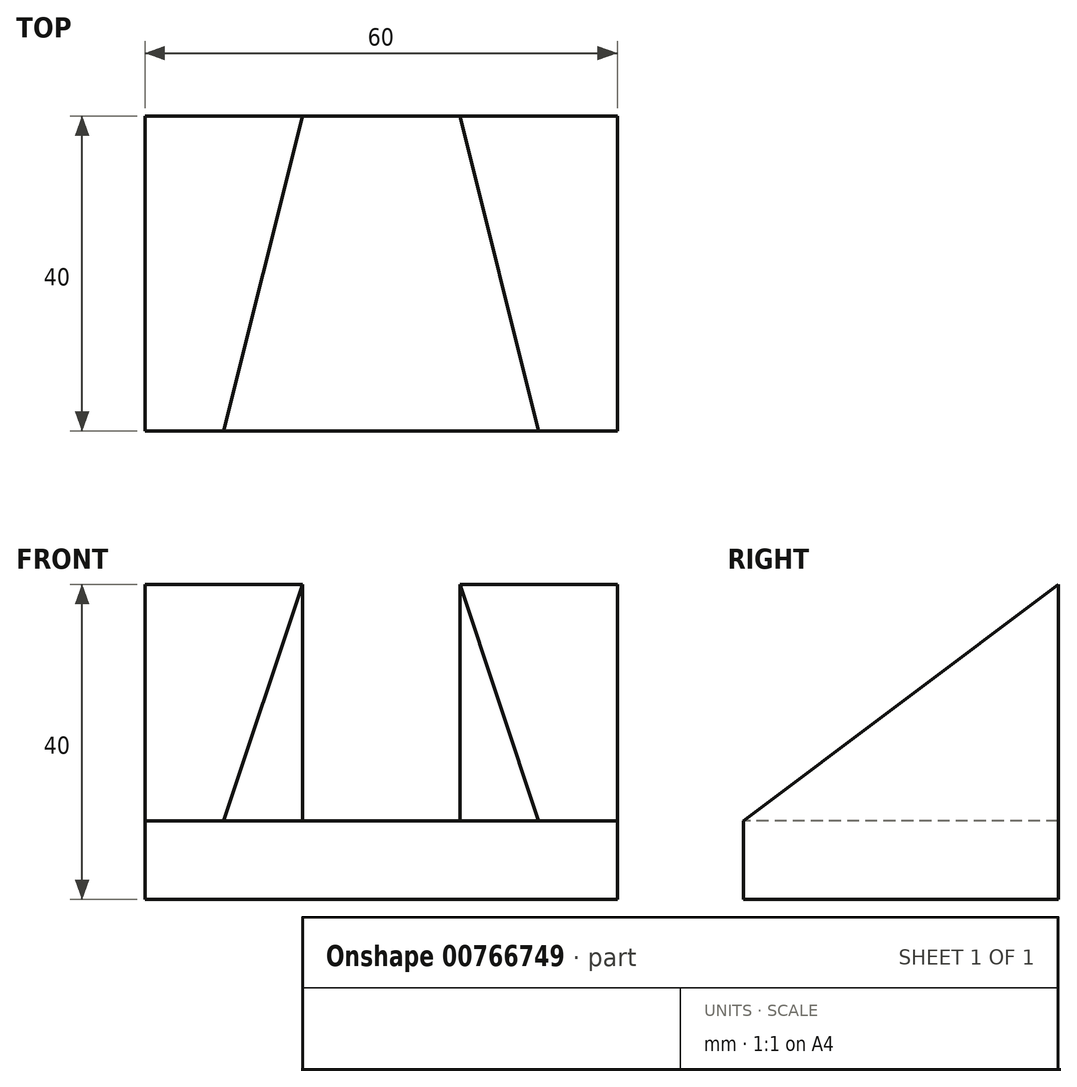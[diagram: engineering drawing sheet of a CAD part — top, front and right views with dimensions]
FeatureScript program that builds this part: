
annotation { "Feature Type Name" : "Feature", "Feature Type Description" : "" }
export const myFeature = defineFeature(function(context is Context, id is Id, definition is map)
    precondition{}
    {
        {
            var Q0;
            Q0=qCreatedBy(makeId("Front.planeOp"),FACE);
            var sketch = newSketch(context, id + "F0", { "sketchPlane" : qUnion([Q0])});
            skLineSegment(sketch, "E0", {"start": v(0, 0) * mm, "end": v(60, 0) * mm});
            skLineSegment(sketch, "E1", {"start": v(60, 0) * mm, "end": v(60, 40) * mm});
            skLineSegment(sketch, "E2", {"start": v(60, 40) * mm, "end": v(0, 40) * mm});
            skLineSegment(sketch, "E3", {"start": v(0, 40) * mm, "end": v(0, 0) * mm});
            skSolve(sketch);
        }
        {
            var Q0;
            Q0 = qSketchRegion(id + "F0", true);
            extrude(context, id + "F1", {"entities" : qUnion([Q0]), "depth" : 40 * mm, "offsetDistance" : 25 * mm});
        }
        {
            var Q0;
            Q0=makeQuery(id+"F1.opExtrude","SWEPT_FACE",FACE,{"disambiguationData":[OSD([sQuery(id+"F0.wireOp",EDGE,"E2")])]});
            var sketch = newSketch(context, id + "F2", { "sketchPlane" : qUnion([Q0])});
            skLineSegment(sketch, "E4", {"start": v(30, -40) * mm, "end": v(30, 0) * mm});
            skLineSegment(sketch, "E5", {"start": v(30, 0) * mm, "end": v(40, 0) * mm});
            skLineSegment(sketch, "E6", {"start": v(40, 0) * mm, "end": v(50, -40) * mm});
            skLineSegment(sketch, "E7", {"start": v(50, -40) * mm, "end": v(30, -40) * mm});
            skSolve(sketch);
        }
        {
            var Q0;
            Q0 = qSketchRegion(id + "F2", true);
            extrude(context, id + "F3", {"entities" : qUnion([Q0]), "operationType" : NewBodyOperationType.REMOVE, "oppositeDirection" : true, "depth" : 30 * mm, "offsetDistance" : 25 * mm});
        }
        {
            var Q0;
            {var subQ0=sQuery(id+"F0.wireOp",EDGE,"E3");var subQ1=sQuery(id+"F0.wireOp",EDGE,"E2");Q0=makeQuery(id+"F3.boolean.opBoolean","SPLIT",FACE,{"disambiguationData":[TD([makeQuery(id+"F1.opExtrude","SWEPT_FACE",FACE,{"disambiguationData":[OSD([subQ0])]})])],"derivedFrom":makeQuery(id+"F1.opExtrude","SWEPT_FACE",FACE,{"disambiguationData":[OSD([subQ1])]})});}
            var sketch = newSketch(context, id + "F4", { "sketchPlane" : qUnion([Q0])});
            skLineSegment(sketch, "E8", {"start": v(30, 0) * mm, "end": v(30, -40) * mm});
            skLineSegment(sketch, "E9", {"start": v(30, -40) * mm, "end": v(10, -40) * mm});
            skLineSegment(sketch, "E10", {"start": v(10, -40) * mm, "end": v(20, 0) * mm});
            skLineSegment(sketch, "E11", {"start": v(20, 0) * mm, "end": v(30, 0) * mm});
            skSolve(sketch);
        }
        {
            var Q0;
            Q0 = qSketchRegion(id + "F4", true);
            extrude(context, id + "F5", {"entities" : qUnion([Q0]), "operationType" : NewBodyOperationType.REMOVE, "oppositeDirection" : true, "depth" : 30 * mm, "offsetDistance" : 25 * mm});
        }
        {
            var Q0;
            Q0=makeQuery(id+"F1.opExtrude","SWEPT_FACE",FACE,{"disambiguationData":[OSD([sQuery(id+"F0.wireOp",EDGE,"E1")])]});
            var sketch = newSketch(context, id + "F6", { "sketchPlane" : qUnion([Q0])});
            skLineSegment(sketch, "E12", {"start": v(0, 40) * mm, "end": v(-40, 10) * mm});
            skLineSegment(sketch, "E13", {"start": v(-40, 10) * mm, "end": v(-40, 40) * mm});
            skLineSegment(sketch, "E14", {"start": v(-40, 40) * mm, "end": v(0, 40) * mm});
            skSolve(sketch);
        }
        {
            var Q0;
            Q0 = qSketchRegion(id + "F6", true);
            extrude(context, id + "F7", {"entities" : qUnion([Q0]), "operationType" : NewBodyOperationType.REMOVE, "oppositeDirection" : true, "depth" : 20 * mm, "offsetDistance" : 25 * mm});
        }
        {
            var Q0;
            Q0=makeQuery(id+"F1.opExtrude","SWEPT_FACE",FACE,{"disambiguationData":[OSD([sQuery(id+"F0.wireOp",EDGE,"E3")])]});
            var sketch = newSketch(context, id + "F8", { "sketchPlane" : qUnion([Q0])});
            skLineSegment(sketch, "E15", {"start": v(0, 40) * mm, "end": v(40, 10) * mm});
            skLineSegment(sketch, "E16", {"start": v(40, 10) * mm, "end": v(40, 40) * mm});
            skLineSegment(sketch, "E17", {"start": v(40, 40) * mm, "end": v(0, 40) * mm});
            skSolve(sketch);
        }
        {
            var Q0;
            Q0 = qSketchRegion(id + "F8", true);
            extrude(context, id + "F9", {"entities" : qUnion([Q0]), "operationType" : NewBodyOperationType.REMOVE, "oppositeDirection" : true, "depth" : 20 * mm, "offsetDistance" : 25 * mm});
        }
    });
